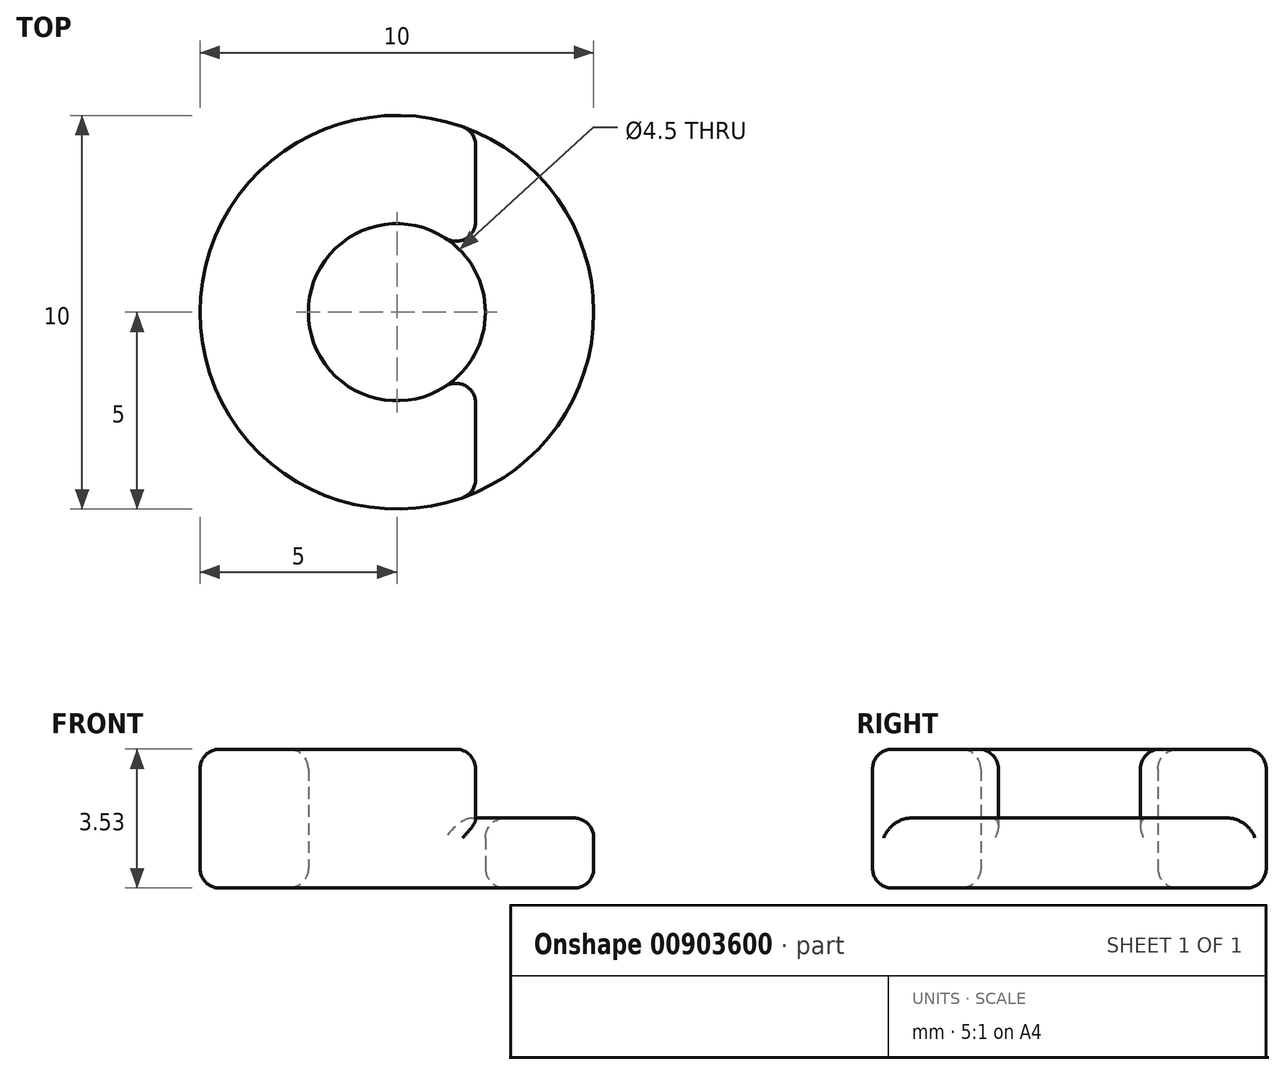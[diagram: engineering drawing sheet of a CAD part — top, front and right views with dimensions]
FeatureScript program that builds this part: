
annotation { "Feature Type Name" : "Feature", "Feature Type Description" : "" }
export const myFeature = defineFeature(function(context is Context, id is Id, definition is map)
    precondition{}
    {
        {
            var Q0;
            Q0=qCreatedBy(makeId("Top.planeOp"),FACE);
            var sketch = newSketch(context, id + "F0", { "sketchPlane" : qUnion([Q0])});
            skCircle(sketch, "E0", {"center": v(0, 0) * mm, "radius": 5 * mm});
            skCircle(sketch, "E1", {"center": v(0, 0) * mm, "radius": 2.25 * mm});
            skSolve(sketch);
        }
        {
            var Q0;
            Q0=makeQuery(id+"F0.imprint","IMPRINT",FACE,{"disambiguationData":[TD([[makeQuery(id+"F0.imprint","IMPRINT",EDGE,{"derivedFrom":sQuery(id+"F0.wireOp",EDGE,"E0")}),1.0]])]});
            extrude(context, id + "F1", {"entities" : qUnion([Q0]), "depth" : 1.78 * mm, "offsetDistance" : 25 * mm});
        }
        {
            var Q0;
            Q0=makeQuery(id+"F1.opExtrude","CAP_FACE",FACE,{"disambiguationData":[OSD([sQuery(id+"F0.wireOp",EDGE,"E0"),sQuery(id+"F0.wireOp",EDGE,"E1")])],"isStart":false});
            var sketch = newSketch(context, id + "F2", { "sketchPlane" : qUnion([Q0])});
            skArc(sketch, "E2", {"start": v(2, 4.58) * mm, "mid": v(-5, 0) * mm, "end": v(2, -4.58) * mm});
            skLineSegment(sketch, "E3", {"start": v(2, 4.58) * mm, "end": v(2, -4.58) * mm});
            skSolve(sketch);
        }
        {
            var Q0;
            Q0=makeQuery(id+"F2.imprint","IMPRINT",FACE,{"disambiguationData":[TD([[makeQuery(id+"F2.imprint","IMPRINT",EDGE,{"derivedFrom":sQuery(id+"F2.wireOp",EDGE,"E2")}),1.0]])]});
            extrude(context, id + "F3", {"entities" : qUnion([Q0]), "operationType" : NewBodyOperationType.ADD, "depth" : 1.75 * mm, "offsetDistance" : 25 * mm});
        }
        {
            var Q0;
            Q0=makeQuery(id+"F3.opExtrude","CAP_EDGE",EDGE,{"disambiguationData":[OSD([sQuery(id+"F2.wireOp",EDGE,"E2")])],"isStart":false});
            var Q1;
            {var subQ0=sQuery(id+"F2.wireOp",EDGE,"E3");var subQ1=sQuery(id+"F0.wireOp",EDGE,"E1");Q1=makeQuery(id+"F3.opExtrude","SWEPT_EDGE",EDGE,{"disambiguationData":[OSD([subQ1,subQ0]),TDD([makeQuery(id+"F2.imprint","INTERSECT",VERTEX,{"disambiguationData":[OD(1.0)],"derivedFrom":[makeQuery(id+"F1.opExtrude","CAP_EDGE",EDGE,{"disambiguationData":[OSD([subQ1])],"isStart":false}),subQ0]})])]});}
            var Q2;
            {var subQ0=sQuery(id+"F2.wireOp",EDGE,"E3");var subQ1=sQuery(id+"F0.wireOp",EDGE,"E1");Q2=makeQuery(id+"F3.opExtrude","SWEPT_EDGE",EDGE,{"disambiguationData":[OSD([subQ1,subQ0]),TDD([makeQuery(id+"F2.imprint","INTERSECT",VERTEX,{"disambiguationData":[OD(0.0)],"derivedFrom":[makeQuery(id+"F1.opExtrude","CAP_EDGE",EDGE,{"disambiguationData":[OSD([subQ1])],"isStart":false}),subQ0]})])]});}
            var Q3;
            {var subQ0=sQuery(id+"F2.wireOp",EDGE,"E3");var subQ1=sQuery(id+"F2.wireOp",EDGE,"E2");var subQ2=sQuery(id+"F0.wireOp",EDGE,"E0");Q3=makeQuery(id+"F3.opExtrude","SWEPT_EDGE",EDGE,{"disambiguationData":[OSD([subQ2,subQ1,subQ0]),TDD([makeQuery(id+"F2.imprint","INTERSECT",VERTEX,{"disambiguationData":[OD(0.0)],"derivedFrom":[makeQuery(id+"F1.opExtrude","CAP_EDGE",EDGE,{"disambiguationData":[OSD([subQ2])],"isStart":false}),subQ1,subQ0]})])]});}
            var Q4;
            {var subQ0=sQuery(id+"F2.wireOp",EDGE,"E3");var subQ1=sQuery(id+"F2.wireOp",EDGE,"E2");var subQ2=sQuery(id+"F0.wireOp",EDGE,"E0");Q4=makeQuery(id+"F3.opExtrude","SWEPT_EDGE",EDGE,{"disambiguationData":[OSD([subQ2,subQ1,subQ0]),TDD([makeQuery(id+"F2.imprint","INTERSECT",VERTEX,{"disambiguationData":[OD(1.0)],"derivedFrom":[makeQuery(id+"F1.opExtrude","CAP_EDGE",EDGE,{"disambiguationData":[OSD([subQ2])],"isStart":false}),subQ1,subQ0]})])]});}
            var Q5;
            Q5=makeQuery(id+"F1.opExtrude","CAP_EDGE",EDGE,{"disambiguationData":[OSD([sQuery(id+"F0.wireOp",EDGE,"E0")])],"isStart":false});
            var Q6;
            Q6=makeQuery(id+"F1.opExtrude","CAP_EDGE",EDGE,{"disambiguationData":[OSD([sQuery(id+"F0.wireOp",EDGE,"E0")])],"isStart":true});
            var Q7;
            Q7=makeQuery(id+"F1.opExtrude","CAP_EDGE",EDGE,{"disambiguationData":[OSD([sQuery(id+"F0.wireOp",EDGE,"E1")])],"isStart":true});
            var Q8;
            Q8=makeQuery(id+"F3.opExtrude","CAP_EDGE",EDGE,{"disambiguationData":[OSD([sQuery(id+"F0.wireOp",EDGE,"E1")])],"isStart":false});
            var Q9;
            Q9=makeQuery(id+"F1.opExtrude","CAP_EDGE",EDGE,{"disambiguationData":[OSD([sQuery(id+"F0.wireOp",EDGE,"E1")])],"isStart":false});
            var Q10;
            {var subQ0=sQuery(id+"F2.wireOp",EDGE,"E3");Q10=makeQuery(id+"F3.opExtrude","CAP_EDGE",EDGE,{"disambiguationData":[OSD([subQ0]),TDD([makeQuery(id+"F2.imprint","IMPRINT",EDGE,{"disambiguationData":[TD([[makeQuery(id+"F2.imprint","INTERSECT",VERTEX,{"disambiguationData":[OD(0.0)],"derivedFrom":[makeQuery(id+"F1.opExtrude","CAP_EDGE",EDGE,{"disambiguationData":[OSD([sQuery(id+"F0.wireOp",EDGE,"E1")])],"isStart":false}),subQ0]}),1.0]])],"derivedFrom":subQ0})])],"isStart":false});}
            var Q11;
            {var subQ0=sQuery(id+"F2.wireOp",EDGE,"E3");Q11=makeQuery(id+"F3.opExtrude","CAP_EDGE",EDGE,{"disambiguationData":[OSD([subQ0]),TDD([makeQuery(id+"F2.imprint","IMPRINT",EDGE,{"disambiguationData":[TD([[makeQuery(id+"F2.imprint","INTERSECT",VERTEX,{"disambiguationData":[OD(1.0)],"derivedFrom":[makeQuery(id+"F1.opExtrude","CAP_EDGE",EDGE,{"disambiguationData":[OSD([sQuery(id+"F0.wireOp",EDGE,"E1")])],"isStart":false}),subQ0]}),-1.0]])],"derivedFrom":subQ0})])],"isStart":false});}
            fillet(context, id + "F4", {"entities" : qUnion([Q0, Q1, Q2, Q3, Q4, Q5, Q6, Q7, Q8, Q9, Q10, Q11]), "radius" : .5 * mm, "tangentPropagation" : true, "allowEdgeOverflow" : false});
        }
    });
